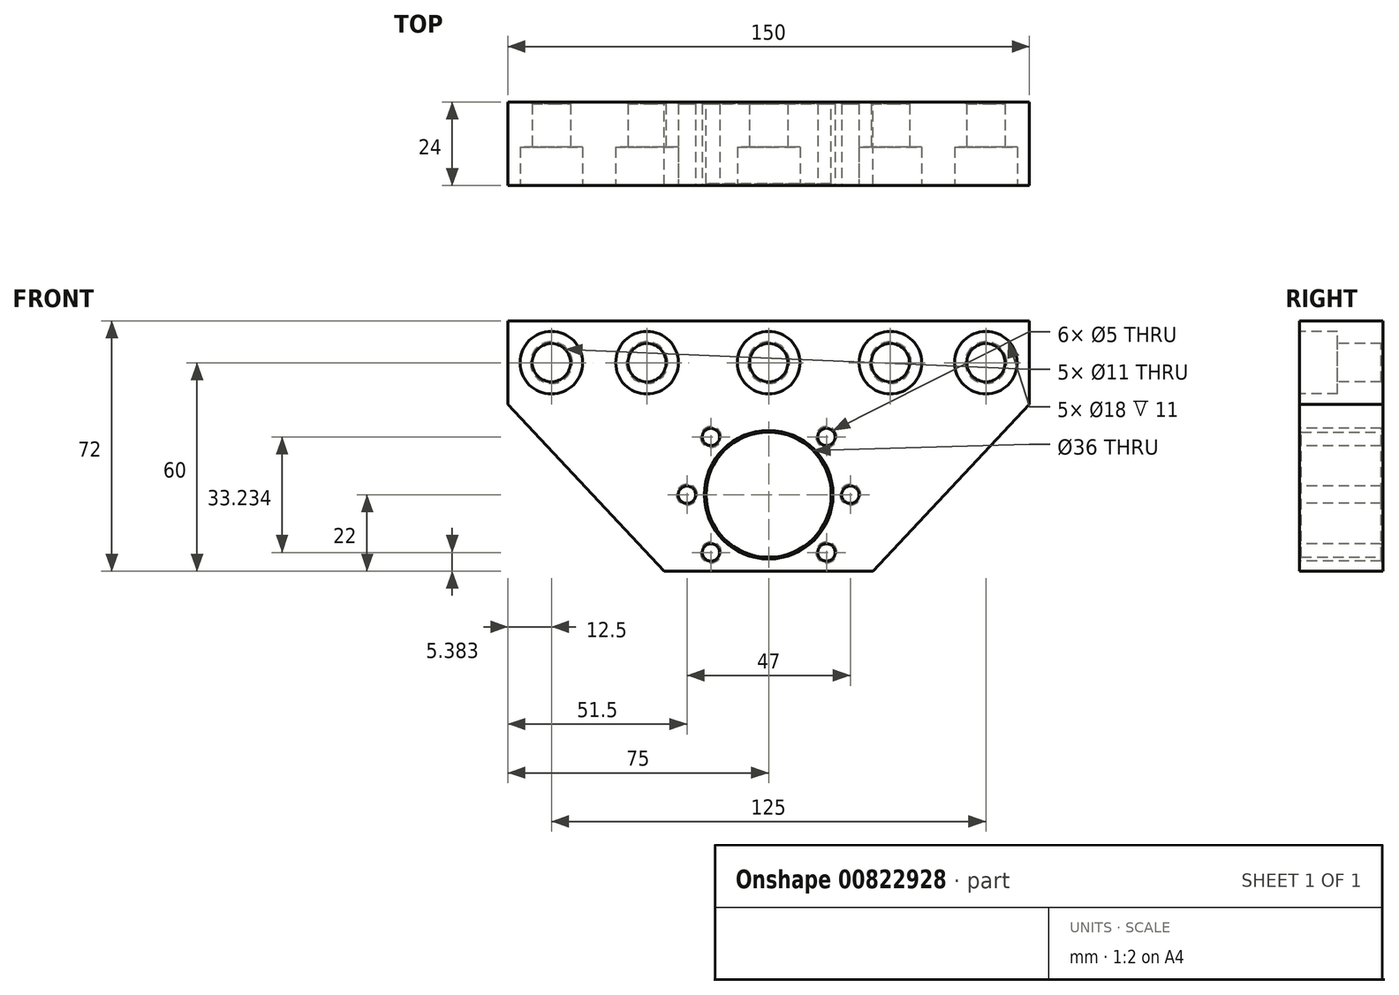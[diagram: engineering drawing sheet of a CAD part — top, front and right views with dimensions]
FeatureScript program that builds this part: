
annotation { "Feature Type Name" : "Feature", "Feature Type Description" : "" }
export const myFeature = defineFeature(function(context is Context, id is Id, definition is map)
    precondition{}
    {
        {
            var Q0;
            Q0=qCreatedBy(makeId("Front.planeOp"),FACE);
            var sketch = newSketch(context, id + "F0", { "sketchPlane" : qUnion([Q0])});
            skCircle(sketch, "E0", {"center": v(0, 0) * mm, "radius": 18 * mm});
            skArc(sketch, "E1", {"start": v(-18.9, 22) * mm, "mid": v(-29, 0) * mm, "end": v(-18.9, -22) * mm, "construction": true});
            skLineSegment(sketch, "E2", {"start": v(0, 0) * mm, "end": v(0, 12) * mm, "construction": true});
            skLineSegment(sketch, "E3", {"start": v(0, 12) * mm, "end": v(-93.5, 12) * mm, "construction": true});
            skLineSegment(sketch, "E4", {"start": v(-93.5, 36) * mm, "end": v(34.56, 36) * mm, "construction": true});
            skLineSegment(sketch, "E5", {"start": v(-93.5, 36) * mm, "end": v(-93.5, 12) * mm, "construction": true});
            skLineSegment(sketch, "E6", {"start": v(-105.7, -10) * mm, "end": v(69, -10) * mm, "construction": true});
            skCircle(sketch, "E7", {"center": v(0, 0) * mm, "radius": 10 * mm, "construction": true});
            skLineSegment(sketch, "E8.bottom", {"start": v(18.9, -22) * mm, "end": v(-18.9, -22) * mm, "construction": true});
            skLineSegment(sketch, "E8.top", {"start": v(18.9, 22) * mm, "end": v(-18.9, 22) * mm, "construction": true});
            skArc(sketch, "E9.trimOffspring", {"start": v(18.9, -22) * mm, "mid": v(29, 0) * mm, "end": v(18.9, 22) * mm, "construction": true});
            skPoint(sketch, "E10.orphan", {"position": v(29, 22) * mm});
            skLineSegment(sketch, "E11.bottom", {"start": v(30, -22) * mm, "end": v(-30, -22) * mm});
            skLineSegment(sketch, "E11.top", {"start": v(30, 30) * mm, "end": v(-30, 30) * mm, "construction": true});
            skLineSegment(sketch, "E11.left", {"start": v(30, -22) * mm, "end": v(30, 30) * mm, "construction": true});
            skLineSegment(sketch, "E11.right", {"start": v(-30, -22) * mm, "end": v(-30, 30) * mm, "construction": true});
            skPoint(sketch, "E11.middle", {"position": v(0, 4) * mm});
            skLineSegment(sketch, "E12", {"start": v(-30, -22) * mm, "end": v(-75, 26) * mm});
            skLineSegment(sketch, "E13", {"start": v(-75, 26) * mm, "end": v(-75, 50) * mm});
            skLineSegment(sketch, "E14", {"start": v(-75, 50) * mm, "end": v(0, 50) * mm});
            skLineSegment(sketch, "E15.MirrorCS", {"start": v(75, 50) * mm, "end": v(0, 50) * mm});
            skLineSegment(sketch, "E16.MirrorCS", {"start": v(75, 26) * mm, "end": v(75, 50) * mm});
            skLineSegment(sketch, "E17.MirrorCS", {"start": v(30, -22) * mm, "end": v(75, 26) * mm});
            skSolve(sketch);
        }
        {
            var Q0;
            Q0 = qSketchRegion(id + "F0", true);
            extrude(context, id + "F1", {"entities" : qUnion([Q0]), "depth" : 24 * mm, "offsetDistance" : 25 * mm});
        }
        {
            var Q0;
            Q0=makeQuery(id+"F1.opExtrude","CAP_FACE",FACE,{"disambiguationData":[OSD([sQuery(id+"F0.wireOp",EDGE,"E0"),sQuery(id+"F0.wireOp",EDGE,"E11.bottom"),sQuery(id+"F0.wireOp",EDGE,"E12"),sQuery(id+"F0.wireOp",EDGE,"E13"),sQuery(id+"F0.wireOp",EDGE,"E14"),sQuery(id+"F0.wireOp",EDGE,"E15.MirrorCS"),sQuery(id+"F0.wireOp",EDGE,"E16.MirrorCS"),sQuery(id+"F0.wireOp",EDGE,"E17.MirrorCS")])],"isStart":false});
            var sketch = newSketch(context, id + "F2", { "sketchPlane" : qUnion([Q0])});
            skLineSegment(sketch, "E18", {"start": v(0, 0) * mm, "end": v(0, 38) * mm, "construction": true});
            skCircle(sketch, "E19", {"center": v(0, 0) * mm, "radius": 23.5 * mm, "construction": true});
            skLineSegment(sketch, "E20", {"start": v(0, 0) * mm, "end": v(-28.4, 0) * mm, "construction": true});
            skCircle(sketch, "E21", {"center": v(-23.5, 0) * mm, "radius": 2.5 * mm});
            skCircle(sketch, "E22.1.0", {"center": v(-16.62, -16.62) * mm, "radius": 2.5 * mm});
            skCircle(sketch, "E22.2.0", {"center": v(0, -23.5) * mm, "radius": 2.5 * mm, "construction": true});
            skCircle(sketch, "E22.3.0", {"center": v(16.62, -16.62) * mm, "radius": 2.5 * mm});
            skCircle(sketch, "E22.4.0", {"center": v(23.5, 0) * mm, "radius": 2.5 * mm});
            skCircle(sketch, "E22.5.0", {"center": v(16.62, 16.62) * mm, "radius": 2.5 * mm});
            skCircle(sketch, "E22.6.0", {"center": v(0, 23.5) * mm, "radius": 2.5 * mm, "construction": true});
            skCircle(sketch, "E22.7.0", {"center": v(-16.62, 16.62) * mm, "radius": 2.5 * mm});
            skCircle(sketch, "E23", {"center": v(0, 0) * mm, "radius": 30 * mm, "construction": true});
            skLineSegment(sketch, "E24", {"start": v(-70.1, 38) * mm, "end": v(0, 38) * mm, "construction": true});
            skCircle(sketch, "E25", {"center": v(-62.5, 38) * mm, "radius": 5.5 * mm});
            skCircle(sketch, "E26", {"center": v(-35, 38) * mm, "radius": 5.5 * mm});
            skCircle(sketch, "E27", {"center": v(-62.5, 38) * mm, "radius": 9 * mm, "construction": true});
            skCircle(sketch, "E28", {"center": v(-35, 38) * mm, "radius": 9 * mm, "construction": true});
            skCircle(sketch, "E29.MirrorC", {"center": v(35, 38) * mm, "radius": 5.5 * mm});
            skCircle(sketch, "E30.MirrorC", {"center": v(62.5, 38) * mm, "radius": 5.5 * mm});
            skCircle(sketch, "E31", {"center": v(0, 38) * mm, "radius": 5.5 * mm});
            skSolve(sketch);
        }
        {
            var Q0;
            Q0 = qSketchRegion(id + "F2", true);
            extrude(context, id + "F3", {"entities" : qUnion([Q0]), "operationType" : NewBodyOperationType.REMOVE, "oppositeDirection" : true, "depth" : 25 * mm, "offsetDistance" : 25 * mm});
        }
        {
            var Q0;
            Q0=makeQuery(id+"F1.opExtrude","CAP_FACE",FACE,{"disambiguationData":[OSD([sQuery(id+"F0.wireOp",EDGE,"E0"),sQuery(id+"F0.wireOp",EDGE,"E11.bottom"),sQuery(id+"F0.wireOp",EDGE,"E12"),sQuery(id+"F0.wireOp",EDGE,"E13"),sQuery(id+"F0.wireOp",EDGE,"E14"),sQuery(id+"F0.wireOp",EDGE,"E15.MirrorCS"),sQuery(id+"F0.wireOp",EDGE,"E16.MirrorCS"),sQuery(id+"F0.wireOp",EDGE,"E17.MirrorCS")])],"isStart":false});
            var sketch = newSketch(context, id + "F4", { "sketchPlane" : qUnion([Q0])});
            skCircle(sketch, "E32", {"center": v(-62.5, 38) * mm, "radius": 9 * mm});
            skCircle(sketch, "E33", {"center": v(-35, 38) * mm, "radius": 9 * mm});
            skLineSegment(sketch, "E34", {"start": v(0, 0) * mm, "end": v(0, 41.38) * mm, "construction": true});
            skCircle(sketch, "E35.MirrorC", {"center": v(62.5, 38) * mm, "radius": 9 * mm});
            skCircle(sketch, "E36.MirrorC", {"center": v(35, 38) * mm, "radius": 9 * mm});
            skCircle(sketch, "E37", {"center": v(0, 38) * mm, "radius": 9 * mm});
            skSolve(sketch);
        }
        {
            var Q0;
            Q0 = qSketchRegion(id + "F4", true);
            extrude(context, id + "F5", {"entities" : qUnion([Q0]), "operationType" : NewBodyOperationType.REMOVE, "oppositeDirection" : true, "depth" : 11 * mm, "offsetDistance" : 25 * mm});
        }
        {
            var Q0;
            Q0=makeQuery(id+"F5.boolean.opBoolean","COPY",EDGE,{"derivedFrom":makeQuery(id+"F5.opExtrude","CAP_EDGE",EDGE,{"disambiguationData":[OSD([sQuery(id+"F4.wireOp",EDGE,"E32")])],"isStart":true})});
            var Q1;
            Q1=makeQuery(id+"F5.boolean.opBoolean","COPY",EDGE,{"derivedFrom":makeQuery(id+"F5.opExtrude","CAP_EDGE",EDGE,{"disambiguationData":[OSD([sQuery(id+"F4.wireOp",EDGE,"E33")])],"isStart":true})});
            var Q2;
            Q2=makeQuery(id+"F3.boolean.opBoolean","COPY",EDGE,{"derivedFrom":makeQuery(id+"F3.opExtrude","CAP_EDGE",EDGE,{"disambiguationData":[OSD([sQuery(id+"F2.wireOp",EDGE,"E22.7.0")])],"isStart":true})});
            var Q3;
            Q3=makeQuery(id+"F3.boolean.opBoolean","COPY",EDGE,{"derivedFrom":makeQuery(id+"F3.opExtrude","CAP_EDGE",EDGE,{"disambiguationData":[OSD([sQuery(id+"F2.wireOp",EDGE,"E21")])],"isStart":true})});
            var Q4;
            Q4=makeQuery(id+"F3.boolean.opBoolean","COPY",EDGE,{"derivedFrom":makeQuery(id+"F3.opExtrude","CAP_EDGE",EDGE,{"disambiguationData":[OSD([sQuery(id+"F2.wireOp",EDGE,"E22.1.0")])],"isStart":true})});
            var Q5;
            Q5=makeQuery(id+"F1.opExtrude","CAP_EDGE",EDGE,{"disambiguationData":[OSD([sQuery(id+"F0.wireOp",EDGE,"E0")])],"isStart":false});
            var Q6;
            Q6=makeQuery(id+"F3.boolean.opBoolean","COPY",EDGE,{"derivedFrom":makeQuery(id+"F3.opExtrude","CAP_EDGE",EDGE,{"disambiguationData":[OSD([sQuery(id+"F2.wireOp",EDGE,"E22.5.0")])],"isStart":true})});
            var Q7;
            Q7=makeQuery(id+"F5.boolean.opBoolean","COPY",EDGE,{"derivedFrom":makeQuery(id+"F5.opExtrude","CAP_EDGE",EDGE,{"disambiguationData":[OSD([sQuery(id+"F4.wireOp",EDGE,"E36.MirrorC")])],"isStart":true})});
            var Q8;
            Q8=makeQuery(id+"F5.boolean.opBoolean","COPY",EDGE,{"derivedFrom":makeQuery(id+"F5.opExtrude","CAP_EDGE",EDGE,{"disambiguationData":[OSD([sQuery(id+"F4.wireOp",EDGE,"E35.MirrorC")])],"isStart":true})});
            var Q9;
            Q9=makeQuery(id+"F3.boolean.opBoolean","COPY",EDGE,{"derivedFrom":makeQuery(id+"F3.opExtrude","CAP_EDGE",EDGE,{"disambiguationData":[OSD([sQuery(id+"F2.wireOp",EDGE,"E22.4.0")])],"isStart":true})});
            var Q10;
            Q10=makeQuery(id+"F3.boolean.opBoolean","COPY",EDGE,{"derivedFrom":makeQuery(id+"F3.opExtrude","CAP_EDGE",EDGE,{"disambiguationData":[OSD([sQuery(id+"F2.wireOp",EDGE,"E22.3.0")])],"isStart":true})});
            var Q11;
            Q11=makeQuery(id+"F3.boolean.opBoolean","INTERSECT",EDGE,{"derivedFrom":[makeQuery(id+"F1.opExtrude","CAP_FACE",FACE,{"disambiguationData":[OSD([sQuery(id+"F0.wireOp",EDGE,"E0"),sQuery(id+"F0.wireOp",EDGE,"E11.bottom"),sQuery(id+"F0.wireOp",EDGE,"E12"),sQuery(id+"F0.wireOp",EDGE,"E13"),sQuery(id+"F0.wireOp",EDGE,"E14"),sQuery(id+"F0.wireOp",EDGE,"E15.MirrorCS"),sQuery(id+"F0.wireOp",EDGE,"E16.MirrorCS"),sQuery(id+"F0.wireOp",EDGE,"E17.MirrorCS")])],"isStart":true}),makeQuery(id+"F3.opExtrude","SWEPT_FACE",FACE,{"disambiguationData":[OSD([sQuery(id+"F2.wireOp",EDGE,"E25")])]})]});
            var Q12;
            Q12=makeQuery(id+"F3.boolean.opBoolean","INTERSECT",EDGE,{"derivedFrom":[makeQuery(id+"F1.opExtrude","CAP_FACE",FACE,{"disambiguationData":[OSD([sQuery(id+"F0.wireOp",EDGE,"E0"),sQuery(id+"F0.wireOp",EDGE,"E11.bottom"),sQuery(id+"F0.wireOp",EDGE,"E12"),sQuery(id+"F0.wireOp",EDGE,"E13"),sQuery(id+"F0.wireOp",EDGE,"E14"),sQuery(id+"F0.wireOp",EDGE,"E15.MirrorCS"),sQuery(id+"F0.wireOp",EDGE,"E16.MirrorCS"),sQuery(id+"F0.wireOp",EDGE,"E17.MirrorCS")])],"isStart":true}),makeQuery(id+"F3.opExtrude","SWEPT_FACE",FACE,{"disambiguationData":[OSD([sQuery(id+"F2.wireOp",EDGE,"E26")])]})]});
            var Q13;
            Q13=makeQuery(id+"F3.boolean.opBoolean","INTERSECT",EDGE,{"derivedFrom":[makeQuery(id+"F1.opExtrude","CAP_FACE",FACE,{"disambiguationData":[OSD([sQuery(id+"F0.wireOp",EDGE,"E0"),sQuery(id+"F0.wireOp",EDGE,"E11.bottom"),sQuery(id+"F0.wireOp",EDGE,"E12"),sQuery(id+"F0.wireOp",EDGE,"E13"),sQuery(id+"F0.wireOp",EDGE,"E14"),sQuery(id+"F0.wireOp",EDGE,"E15.MirrorCS"),sQuery(id+"F0.wireOp",EDGE,"E16.MirrorCS"),sQuery(id+"F0.wireOp",EDGE,"E17.MirrorCS")])],"isStart":true}),makeQuery(id+"F3.opExtrude","SWEPT_FACE",FACE,{"disambiguationData":[OSD([sQuery(id+"F2.wireOp",EDGE,"E22.7.0")])]})]});
            var Q14;
            Q14=makeQuery(id+"F3.boolean.opBoolean","INTERSECT",EDGE,{"derivedFrom":[makeQuery(id+"F1.opExtrude","CAP_FACE",FACE,{"disambiguationData":[OSD([sQuery(id+"F0.wireOp",EDGE,"E0"),sQuery(id+"F0.wireOp",EDGE,"E11.bottom"),sQuery(id+"F0.wireOp",EDGE,"E12"),sQuery(id+"F0.wireOp",EDGE,"E13"),sQuery(id+"F0.wireOp",EDGE,"E14"),sQuery(id+"F0.wireOp",EDGE,"E15.MirrorCS"),sQuery(id+"F0.wireOp",EDGE,"E16.MirrorCS"),sQuery(id+"F0.wireOp",EDGE,"E17.MirrorCS")])],"isStart":true}),makeQuery(id+"F3.opExtrude","SWEPT_FACE",FACE,{"disambiguationData":[OSD([sQuery(id+"F2.wireOp",EDGE,"E21")])]})]});
            var Q15;
            Q15=makeQuery(id+"F3.boolean.opBoolean","INTERSECT",EDGE,{"derivedFrom":[makeQuery(id+"F1.opExtrude","CAP_FACE",FACE,{"disambiguationData":[OSD([sQuery(id+"F0.wireOp",EDGE,"E0"),sQuery(id+"F0.wireOp",EDGE,"E11.bottom"),sQuery(id+"F0.wireOp",EDGE,"E12"),sQuery(id+"F0.wireOp",EDGE,"E13"),sQuery(id+"F0.wireOp",EDGE,"E14"),sQuery(id+"F0.wireOp",EDGE,"E15.MirrorCS"),sQuery(id+"F0.wireOp",EDGE,"E16.MirrorCS"),sQuery(id+"F0.wireOp",EDGE,"E17.MirrorCS")])],"isStart":true}),makeQuery(id+"F3.opExtrude","SWEPT_FACE",FACE,{"disambiguationData":[OSD([sQuery(id+"F2.wireOp",EDGE,"E22.1.0")])]})]});
            var Q16;
            Q16=makeQuery(id+"F1.opExtrude","CAP_EDGE",EDGE,{"disambiguationData":[OSD([sQuery(id+"F0.wireOp",EDGE,"E0")])],"isStart":true});
            var Q17;
            Q17=makeQuery(id+"F3.boolean.opBoolean","INTERSECT",EDGE,{"derivedFrom":[makeQuery(id+"F1.opExtrude","CAP_FACE",FACE,{"disambiguationData":[OSD([sQuery(id+"F0.wireOp",EDGE,"E0"),sQuery(id+"F0.wireOp",EDGE,"E11.bottom"),sQuery(id+"F0.wireOp",EDGE,"E12"),sQuery(id+"F0.wireOp",EDGE,"E13"),sQuery(id+"F0.wireOp",EDGE,"E14"),sQuery(id+"F0.wireOp",EDGE,"E15.MirrorCS"),sQuery(id+"F0.wireOp",EDGE,"E16.MirrorCS"),sQuery(id+"F0.wireOp",EDGE,"E17.MirrorCS")])],"isStart":true}),makeQuery(id+"F3.opExtrude","SWEPT_FACE",FACE,{"disambiguationData":[OSD([sQuery(id+"F2.wireOp",EDGE,"E22.3.0")])]})]});
            var Q18;
            Q18=makeQuery(id+"F3.boolean.opBoolean","INTERSECT",EDGE,{"derivedFrom":[makeQuery(id+"F1.opExtrude","CAP_FACE",FACE,{"disambiguationData":[OSD([sQuery(id+"F0.wireOp",EDGE,"E0"),sQuery(id+"F0.wireOp",EDGE,"E11.bottom"),sQuery(id+"F0.wireOp",EDGE,"E12"),sQuery(id+"F0.wireOp",EDGE,"E13"),sQuery(id+"F0.wireOp",EDGE,"E14"),sQuery(id+"F0.wireOp",EDGE,"E15.MirrorCS"),sQuery(id+"F0.wireOp",EDGE,"E16.MirrorCS"),sQuery(id+"F0.wireOp",EDGE,"E17.MirrorCS")])],"isStart":true}),makeQuery(id+"F3.opExtrude","SWEPT_FACE",FACE,{"disambiguationData":[OSD([sQuery(id+"F2.wireOp",EDGE,"E22.4.0")])]})]});
            var Q19;
            Q19=makeQuery(id+"F3.boolean.opBoolean","INTERSECT",EDGE,{"derivedFrom":[makeQuery(id+"F1.opExtrude","CAP_FACE",FACE,{"disambiguationData":[OSD([sQuery(id+"F0.wireOp",EDGE,"E0"),sQuery(id+"F0.wireOp",EDGE,"E11.bottom"),sQuery(id+"F0.wireOp",EDGE,"E12"),sQuery(id+"F0.wireOp",EDGE,"E13"),sQuery(id+"F0.wireOp",EDGE,"E14"),sQuery(id+"F0.wireOp",EDGE,"E15.MirrorCS"),sQuery(id+"F0.wireOp",EDGE,"E16.MirrorCS"),sQuery(id+"F0.wireOp",EDGE,"E17.MirrorCS")])],"isStart":true}),makeQuery(id+"F3.opExtrude","SWEPT_FACE",FACE,{"disambiguationData":[OSD([sQuery(id+"F2.wireOp",EDGE,"E22.5.0")])]})]});
            var Q20;
            Q20=makeQuery(id+"F3.boolean.opBoolean","INTERSECT",EDGE,{"derivedFrom":[makeQuery(id+"F1.opExtrude","CAP_FACE",FACE,{"disambiguationData":[OSD([sQuery(id+"F0.wireOp",EDGE,"E0"),sQuery(id+"F0.wireOp",EDGE,"E11.bottom"),sQuery(id+"F0.wireOp",EDGE,"E12"),sQuery(id+"F0.wireOp",EDGE,"E13"),sQuery(id+"F0.wireOp",EDGE,"E14"),sQuery(id+"F0.wireOp",EDGE,"E15.MirrorCS"),sQuery(id+"F0.wireOp",EDGE,"E16.MirrorCS"),sQuery(id+"F0.wireOp",EDGE,"E17.MirrorCS")])],"isStart":true}),makeQuery(id+"F3.opExtrude","SWEPT_FACE",FACE,{"disambiguationData":[OSD([sQuery(id+"F2.wireOp",EDGE,"E29.MirrorC")])]})]});
            var Q21;
            Q21=makeQuery(id+"F3.boolean.opBoolean","INTERSECT",EDGE,{"derivedFrom":[makeQuery(id+"F1.opExtrude","CAP_FACE",FACE,{"disambiguationData":[OSD([sQuery(id+"F0.wireOp",EDGE,"E0"),sQuery(id+"F0.wireOp",EDGE,"E11.bottom"),sQuery(id+"F0.wireOp",EDGE,"E12"),sQuery(id+"F0.wireOp",EDGE,"E13"),sQuery(id+"F0.wireOp",EDGE,"E14"),sQuery(id+"F0.wireOp",EDGE,"E15.MirrorCS"),sQuery(id+"F0.wireOp",EDGE,"E16.MirrorCS"),sQuery(id+"F0.wireOp",EDGE,"E17.MirrorCS")])],"isStart":true}),makeQuery(id+"F3.opExtrude","SWEPT_FACE",FACE,{"disambiguationData":[OSD([sQuery(id+"F2.wireOp",EDGE,"E30.MirrorC")])]})]});
            var Q22;
            Q22=makeQuery(id+"F5.boolean.opBoolean","COPY",EDGE,{"derivedFrom":makeQuery(id+"F5.opExtrude","CAP_EDGE",EDGE,{"disambiguationData":[OSD([sQuery(id+"F4.wireOp",EDGE,"E37")])],"isStart":true})});
            var Q23;
            Q23=makeQuery(id+"F3.boolean.opBoolean","INTERSECT",EDGE,{"derivedFrom":[makeQuery(id+"F1.opExtrude","CAP_FACE",FACE,{"disambiguationData":[OSD([sQuery(id+"F0.wireOp",EDGE,"E0"),sQuery(id+"F0.wireOp",EDGE,"E11.bottom"),sQuery(id+"F0.wireOp",EDGE,"E12"),sQuery(id+"F0.wireOp",EDGE,"E13"),sQuery(id+"F0.wireOp",EDGE,"E14"),sQuery(id+"F0.wireOp",EDGE,"E15.MirrorCS"),sQuery(id+"F0.wireOp",EDGE,"E16.MirrorCS"),sQuery(id+"F0.wireOp",EDGE,"E17.MirrorCS")])],"isStart":true}),makeQuery(id+"F3.opExtrude","SWEPT_FACE",FACE,{"disambiguationData":[OSD([sQuery(id+"F2.wireOp",EDGE,"E31")])]})]});
            chamfer(context, id + "F6", {"entities" : qUnion([Q0, Q1, Q2, Q3, Q4, Q5, Q6, Q7, Q8, Q9, Q10, Q11, Q12, Q13, Q14, Q15, Q16, Q17, Q18, Q19, Q20, Q21, Q22, Q23]), "width" : 0.5 * mm, "tangentPropagation" : true});
        }
    });
